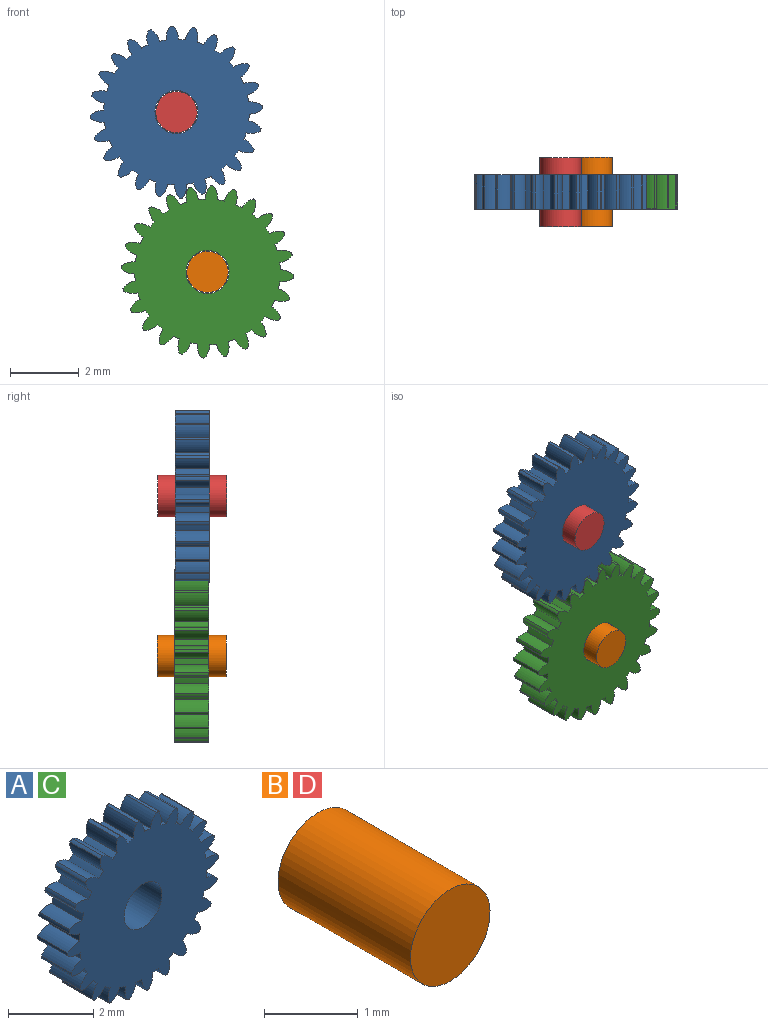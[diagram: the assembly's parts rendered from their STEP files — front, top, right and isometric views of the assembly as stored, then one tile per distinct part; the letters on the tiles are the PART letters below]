
ASSEMBLY  parts=4 mates=2
PART A: 99 faces, bbox 5x1x5 mm
  f0: cylinder r=2.12mm len=1mm, axis (0,1,0), area 0.2mm2, adj f28,f29,f68,f71
  f1: cylinder r=2.12mm len=1mm, axis (0,1,0), area 0.2mm2, adj f28,f29,f70,f74
  f2: cylinder r=2.12mm len=1mm, axis (0,1,0), area 0.2mm2, adj f28,f29,f73,f77
  f3: cylinder r=2.12mm len=1mm, axis (0,1,0), area 0.2mm2, adj f28,f29,f76,f80
  f4: cylinder r=2.12mm len=1mm, axis (0,1,0), area 0.2mm2, adj f28,f29,f79,f83
  f5: cylinder r=2.12mm len=1mm, axis (0,1,0), area 0.2mm2, adj f28,f29,f82,f86
  f6: cylinder r=2.12mm len=1mm, axis (0,1,0), area 0.2mm2, adj f28,f29,f85,f89
  f7: cylinder r=2.12mm len=1mm, axis (0,1,0), area 0.2mm2, adj f28,f29,f88,f92
  f8: cylinder r=2.12mm len=1mm, axis (0,1,0), area 0.2mm2, adj f28,f29,f91,f95
  f9: cylinder r=2.12mm len=1mm, axis (0,1,0), area 0.2mm2, adj f28,f29,f94,f98
  f10: cylinder r=2.12mm len=1mm, axis (0,1,0), area 0.2mm2, adj f28,f29,f32,f96
  f11: cylinder r=2.12mm len=1mm, axis (0,1,0), area 0.2mm2, adj f28,f29,f31,f35
  f12: cylinder r=2.12mm len=1mm, axis (0,1,0), area 0.2mm2, adj f28,f29,f34,f38
  f13: cylinder r=2.12mm len=1mm, axis (0,1,0), area 0.2mm2, adj f28,f29,f37,f41
  f14: cylinder r=2.12mm len=1mm, axis (0,1,0), area 0.2mm2, adj f28,f29,f40,f44
  f15: cylinder r=2.12mm len=1mm, axis (0,1,0), area 0.2mm2, adj f28,f29,f43,f47
  f16: cylinder r=2.12mm len=1mm, axis (0,1,0), area 0.2mm2, adj f28,f29,f46,f50
  f17: cylinder r=2.12mm len=1mm, axis (0,1,0), area 0.2mm2, adj f28,f29,f49,f53
  f18: cylinder r=2.12mm len=1mm, axis (0,1,0), area 0.2mm2, adj f28,f29,f52,f56
  f19: cylinder r=2.12mm len=1mm, axis (0,1,0), area 0.2mm2, adj f28,f29,f55,f59
  f20: cylinder r=2.12mm len=1mm, axis (0,1,0), area 0.2mm2, adj f28,f29,f58,f62
  f21: cylinder r=2.12mm len=1mm, axis (0,1,0), area 0.2mm2, adj f28,f29,f61,f65
  f22: cylinder r=2.12mm len=1mm, axis (0,1,0), area 0.2mm2, adj f27,f28,f29,f64
  f23: cylinder r=2.12mm len=1mm, axis (0,1,0), area 0.2mm2, adj f24,f28,f29,f67
  f24: cylinder r=0.58mm len=1mm, axis (0,1,0), area 0.4mm2, adj f23,f25,f28,f29
  f25: cylinder r=0.25mm len=1mm, axis (0,1,0), area 0.1mm2, adj f24,f27,f28,f29
  f26: cylinder r=0.62mm len=1.25mm, axis (0,1,0), area 3.9mm2, adj f28,f29
  f27: cylinder r=0.58mm len=1mm, axis (0,1,0), area 0.4mm2, adj f22,f25,f28,f29
  f28: plane 5x5mm, normal (0,-1,0), area 15.4mm2, adj f0,f1,f2,f3,f4,f5,f6,f7
  f29: plane 5x5mm, normal (0,1,0), area 15.4mm2, adj f0,f1,f2,f3,f4,f5,f6,f7
  f30: cylinder r=0.25mm len=1mm, axis (0,1,0), area 0.1mm2, adj f28,f29,f31,f32
  f31: cylinder r=0.58mm len=1mm, axis (0,1,0), area 0.4mm2, adj f11,f28,f29,f30
  f32: cylinder r=0.58mm len=1mm, axis (0,1,0), area 0.4mm2, adj f10,f28,f29,f30
  f33: cylinder r=0.25mm len=1mm, axis (0,1,0), area 0.1mm2, adj f28,f29,f34,f35
  f34: cylinder r=0.58mm len=1mm, axis (0,1,0), area 0.4mm2, adj f12,f28,f29,f33
  f35: cylinder r=0.58mm len=1mm, axis (0,1,0), area 0.4mm2, adj f11,f28,f29,f33
  f36: cylinder r=0.25mm len=1mm, axis (0,1,0), area 0.1mm2, adj f28,f29,f37,f38
  f37: cylinder r=0.58mm len=1mm, axis (0,1,0), area 0.4mm2, adj f13,f28,f29,f36
  f38: cylinder r=0.58mm len=1mm, axis (0,1,0), area 0.4mm2, adj f12,f28,f29,f36
  f39: cylinder r=0.25mm len=1mm, axis (0,1,0), area 0.1mm2, adj f28,f29,f40,f41
  f40: cylinder r=0.58mm len=1mm, axis (0,1,0), area 0.4mm2, adj f14,f28,f29,f39
  f41: cylinder r=0.58mm len=1mm, axis (0,1,0), area 0.4mm2, adj f13,f28,f29,f39
  f42: cylinder r=0.25mm len=1mm, axis (0,1,0), area 0.1mm2, adj f28,f29,f43,f44
  f43: cylinder r=0.58mm len=1mm, axis (0,1,0), area 0.4mm2, adj f15,f28,f29,f42
  f44: cylinder r=0.58mm len=1mm, axis (0,1,0), area 0.4mm2, adj f14,f28,f29,f42
  f45: cylinder r=0.25mm len=1mm, axis (0,1,0), area 0.1mm2, adj f28,f29,f46,f47
  f46: cylinder r=0.58mm len=1mm, axis (0,1,0), area 0.4mm2, adj f16,f28,f29,f45
  f47: cylinder r=0.58mm len=1mm, axis (0,1,0), area 0.4mm2, adj f15,f28,f29,f45
  f48: cylinder r=0.25mm len=1mm, axis (0,1,0), area 0.1mm2, adj f28,f29,f49,f50
  f49: cylinder r=0.58mm len=1mm, axis (0,1,0), area 0.4mm2, adj f17,f28,f29,f48
  f50: cylinder r=0.58mm len=1mm, axis (0,1,0), area 0.4mm2, adj f16,f28,f29,f48
  f51: cylinder r=0.25mm len=1mm, axis (0,1,0), area 0.1mm2, adj f28,f29,f52,f53
  f52: cylinder r=0.58mm len=1mm, axis (0,1,0), area 0.4mm2, adj f18,f28,f29,f51
  f53: cylinder r=0.58mm len=1mm, axis (0,1,0), area 0.4mm2, adj f17,f28,f29,f51
  f54: cylinder r=0.25mm len=1mm, axis (0,1,0), area 0.1mm2, adj f28,f29,f55,f56
  f55: cylinder r=0.58mm len=1mm, axis (0,1,0), area 0.4mm2, adj f19,f28,f29,f54
  f56: cylinder r=0.58mm len=1mm, axis (0,1,0), area 0.4mm2, adj f18,f28,f29,f54
  f57: cylinder r=0.25mm len=1mm, axis (0,1,0), area 0.1mm2, adj f28,f29,f58,f59
  f58: cylinder r=0.58mm len=1mm, axis (0,1,0), area 0.4mm2, adj f20,f28,f29,f57
  f59: cylinder r=0.58mm len=1mm, axis (0,1,0), area 0.4mm2, adj f19,f28,f29,f57
  f60: cylinder r=0.25mm len=1mm, axis (0,1,0), area 0.1mm2, adj f28,f29,f61,f62
  f61: cylinder r=0.58mm len=1mm, axis (0,1,0), area 0.4mm2, adj f21,f28,f29,f60
  f62: cylinder r=0.58mm len=1mm, axis (0,1,0), area 0.4mm2, adj f20,f28,f29,f60
  f63: cylinder r=0.25mm len=1mm, axis (0,1,0), area 0.1mm2, adj f28,f29,f64,f65
  f64: cylinder r=0.58mm len=1mm, axis (0,1,0), area 0.4mm2, adj f22,f28,f29,f63
  f65: cylinder r=0.58mm len=1mm, axis (0,1,0), area 0.4mm2, adj f21,f28,f29,f63
  f66: cylinder r=0.25mm len=1mm, axis (0,1,0), area 0.1mm2, adj f28,f29,f67,f68
  f67: cylinder r=0.58mm len=1mm, axis (0,1,0), area 0.4mm2, adj f23,f28,f29,f66
  f68: cylinder r=0.58mm len=1mm, axis (0,1,0), area 0.4mm2, adj f0,f28,f29,f66
  f69: cylinder r=0.25mm len=1mm, axis (0,1,0), area 0.1mm2, adj f28,f29,f70,f71
  f70: cylinder r=0.58mm len=1mm, axis (0,1,0), area 0.4mm2, adj f1,f28,f29,f69
  f71: cylinder r=0.58mm len=1mm, axis (0,1,0), area 0.4mm2, adj f0,f28,f29,f69
  f72: cylinder r=0.25mm len=1mm, axis (0,1,0), area 0.1mm2, adj f28,f29,f73,f74
  f73: cylinder r=0.58mm len=1mm, axis (0,1,0), area 0.4mm2, adj f2,f28,f29,f72
  f74: cylinder r=0.58mm len=1mm, axis (0,1,0), area 0.4mm2, adj f1,f28,f29,f72
  f75: cylinder r=0.25mm len=1mm, axis (0,1,0), area 0.1mm2, adj f28,f29,f76,f77
  f76: cylinder r=0.58mm len=1mm, axis (0,1,0), area 0.4mm2, adj f3,f28,f29,f75
  f77: cylinder r=0.58mm len=1mm, axis (0,1,0), area 0.4mm2, adj f2,f28,f29,f75
  f78: cylinder r=0.25mm len=1mm, axis (0,1,0), area 0.1mm2, adj f28,f29,f79,f80
  f79: cylinder r=0.58mm len=1mm, axis (0,1,0), area 0.4mm2, adj f4,f28,f29,f78
  f80: cylinder r=0.58mm len=1mm, axis (0,1,0), area 0.4mm2, adj f3,f28,f29,f78
  f81: cylinder r=0.25mm len=1mm, axis (0,1,0), area 0.1mm2, adj f28,f29,f82,f83
  f82: cylinder r=0.58mm len=1mm, axis (0,1,0), area 0.4mm2, adj f5,f28,f29,f81
  f83: cylinder r=0.58mm len=1mm, axis (0,1,0), area 0.4mm2, adj f4,f28,f29,f81
  f84: cylinder r=0.25mm len=1mm, axis (0,1,0), area 0.1mm2, adj f28,f29,f85,f86
  f85: cylinder r=0.58mm len=1mm, axis (0,1,0), area 0.4mm2, adj f6,f28,f29,f84
  f86: cylinder r=0.58mm len=1mm, axis (0,1,0), area 0.4mm2, adj f5,f28,f29,f84
  f87: cylinder r=0.25mm len=1mm, axis (0,1,0), area 0.1mm2, adj f28,f29,f88,f89
  f88: cylinder r=0.58mm len=1mm, axis (0,1,0), area 0.4mm2, adj f7,f28,f29,f87
  f89: cylinder r=0.58mm len=1mm, axis (0,1,0), area 0.4mm2, adj f6,f28,f29,f87
  f90: cylinder r=0.25mm len=1mm, axis (0,1,0), area 0.1mm2, adj f28,f29,f91,f92
  f91: cylinder r=0.58mm len=1mm, axis (0,1,0), area 0.4mm2, adj f8,f28,f29,f90
  f92: cylinder r=0.58mm len=1mm, axis (0,1,0), area 0.4mm2, adj f7,f28,f29,f90
  f93: cylinder r=0.25mm len=1mm, axis (0,1,0), area 0.1mm2, adj f28,f29,f94,f95
  f94: cylinder r=0.58mm len=1mm, axis (0,1,0), area 0.4mm2, adj f9,f28,f29,f93
  f95: cylinder r=0.58mm len=1mm, axis (0,1,0), area 0.4mm2, adj f8,f28,f29,f93
  f96: cylinder r=0.58mm len=1mm, axis (0,1,0), area 0.4mm2, adj f10,f28,f29,f97
  f97: cylinder r=0.25mm len=1mm, axis (0,1,0), area 0.1mm2, adj f28,f29,f96,f98
  f98: cylinder r=0.58mm len=1mm, axis (0,1,0), area 0.4mm2, adj f9,f28,f29,f97
PART B: 3 faces, bbox 1.2x2x1.2 mm
  f0: cylinder r=0.6mm len=2mm, axis (0,1,0), area 7.5mm2, adj f1,f2
  f1: plane 1.2x1.2mm, normal (0,-1,0), area 1.1mm2, adj f0
  f2: plane 1.2x1.2mm, normal (0,1,0), area 1.1mm2, adj f0
PART C: same geometry as A
PART D: same geometry as B
PLACE A rot(axis=(0,1,0),105.6deg) t=(-0.01,0.5,0.02)mm
PLACE B rot(axis=(0,-1,0),7.6deg) t=(0.9,1.02,-4.63)mm fixed
PLACE C rot(axis=(0,-1,0),113.2deg) t=(0.9,0.52,-4.63)mm
PLACE D t=(-0.01,1,0.02)mm fixed
MATE revolute C.f26 <-> B.f0  axis (0,1,0) through (0.9,0.02,-4.63)mm
MATE revolute D.f0 <-> A.f26  axis (0,1,0) through (-0.01,0,0.02)mm
